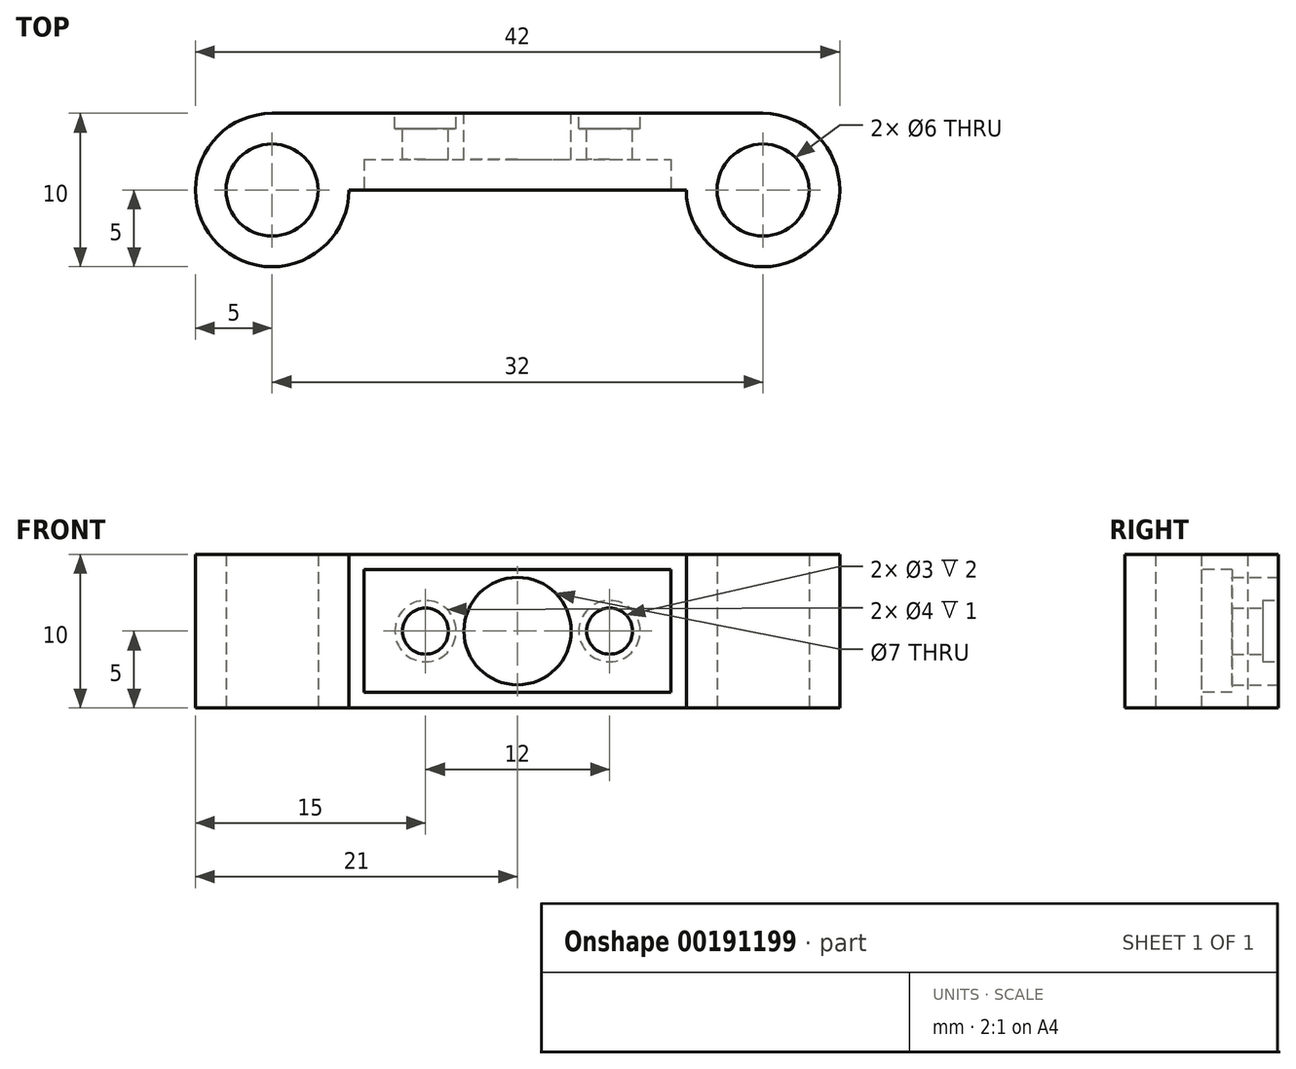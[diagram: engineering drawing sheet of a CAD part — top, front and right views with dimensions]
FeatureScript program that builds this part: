
annotation { "Feature Type Name" : "Feature", "Feature Type Description" : "" }
export const myFeature = defineFeature(function(context is Context, id is Id, definition is map)
    precondition{}
    {
        {
            var Q0;
            Q0=qCreatedBy(makeId("Top.planeOp"),FACE);
            var sketch = newSketch(context, id + "F0", { "sketchPlane" : qUnion([Q0])});
            skCircle(sketch, "E0", {"center": v(-16, 0) * mm, "radius": 3 * mm});
            skCircle(sketch, "E1", {"center": v(16, 0) * mm, "radius": 3 * mm});
            skCircle(sketch, "E2", {"center": v(-16, 0) * mm, "radius": 5 * mm});
            skCircle(sketch, "E3", {"center": v(16, 0) * mm, "radius": 5 * mm});
            skLineSegment(sketch, "E4", {"start": v(-16, 5) * mm, "end": v(16, 5) * mm});
            skLineSegment(sketch, "E5.0", {"start": v(-16.5, 0) * mm, "end": v(16.5, 0) * mm});
            skSolve(sketch);
        }
        {
            var Q0;
            Q0 = qSketchRegion(id + "F0", true);
            extrude(context, id + "F1", {"entities" : qUnion([Q0]), "depth" : 10 * mm});
        }
        {
            var Q0;
            Q0=makeQuery(id+"F1.opExtrude","SWEPT_FACE",FACE,{"disambiguationData":[OSD([sQuery(id+"F0.wireOp",EDGE,"E5.0")])]});
            var sketch = newSketch(context, id + "F2", { "sketchPlane" : qUnion([Q0])});
            skLineSegment(sketch, "E6.0", {"start": v(-11, 10) * mm, "end": v(-11, 0) * mm});
            skLineSegment(sketch, "E6.1", {"start": v(-11, 10) * mm, "end": v(11, 10) * mm});
            skLineSegment(sketch, "E6.2", {"start": v(11, 10) * mm, "end": v(11, 0) * mm});
            skLineSegment(sketch, "E6.3", {"start": v(-11, 0) * mm, "end": v(11, 0) * mm});
            skPoint(sketch, "E6.4", {"position": v(11, 5) * mm});
            skLineSegment(sketch, "E7.0", {"start": v(-10, 9) * mm, "end": v(10, 9) * mm});
            skLineSegment(sketch, "E8.0", {"start": v(-10, 9) * mm, "end": v(-10, 1) * mm});
            skLineSegment(sketch, "E9.0", {"start": v(-10, 1) * mm, "end": v(10, 1) * mm});
            skLineSegment(sketch, "E10.0", {"start": v(10, 9) * mm, "end": v(10, 1) * mm});
            skSolve(sketch);
        }
        {
            var Q0;
            Q0=makeQuery(id+"F2.imprint","IMPRINT",FACE,{"disambiguationData":[TD([[makeQuery(id+"F2.imprint","IMPRINT",EDGE,{"derivedFrom":sQuery(id+"F2.wireOp",EDGE,"E7.0")}),-1.0]])]});
            extrude(context, id + "F3", {"entities" : qUnion([Q0]), "operationType" : NewBodyOperationType.REMOVE, "oppositeDirection" : true, "depth" : 2 * mm});
        }
        {
            var Q0;
            Q0=makeQuery(id+"F1.opExtrude","SWEPT_FACE",FACE,{"disambiguationData":[OSD([sQuery(id+"F0.wireOp",EDGE,"E4")])]});
            var sketch = newSketch(context, id + "F4", { "sketchPlane" : qUnion([Q0])});
            skLineSegment(sketch, "E11.0", {"start": v(16, 10) * mm, "end": v(-16, 10) * mm});
            skLineSegment(sketch, "E11.1", {"start": v(16, 10) * mm, "end": v(16, 0) * mm});
            skLineSegment(sketch, "E12", {"start": v(0, 10) * mm, "end": v(0, 0) * mm});
            skCircle(sketch, "E13", {"center": v(0, 5) * mm, "radius": 3.5 * mm});
            skCircle(sketch, "E14", {"center": v(6, 5) * mm, "radius": 1.5 * mm});
            skCircle(sketch, "E15", {"center": v(-6, 5) * mm, "radius": 1.5 * mm});
            skSolve(sketch);
        }
        {
            var Q0;
            Q0 = qSketchRegion(id + "F4", true);
            extrude(context, id + "F5", {"entities" : qUnion([Q0]), "operationType" : NewBodyOperationType.REMOVE, "oppositeDirection" : true, "depth" : 5 * mm});
        }
        {
            var Q0;
            Q0=makeQuery(id+"F1.opExtrude","SWEPT_FACE",FACE,{"disambiguationData":[OSD([sQuery(id+"F0.wireOp",EDGE,"E4")])]});
            var sketch = newSketch(context, id + "F6", { "sketchPlane" : qUnion([Q0])});
            skCircle(sketch, "E16", {"center": v(-6, 5) * mm, "radius": 2 * mm});
            skCircle(sketch, "E17", {"center": v(6, 5) * mm, "radius": 2 * mm});
            skSolve(sketch);
        }
        {
            var Q0;
            Q0 = qSketchRegion(id + "F6", true);
            extrude(context, id + "F7", {"entities" : qUnion([Q0]), "operationType" : NewBodyOperationType.REMOVE, "oppositeDirection" : true, "depth" : 1 * mm});
        }
    });
